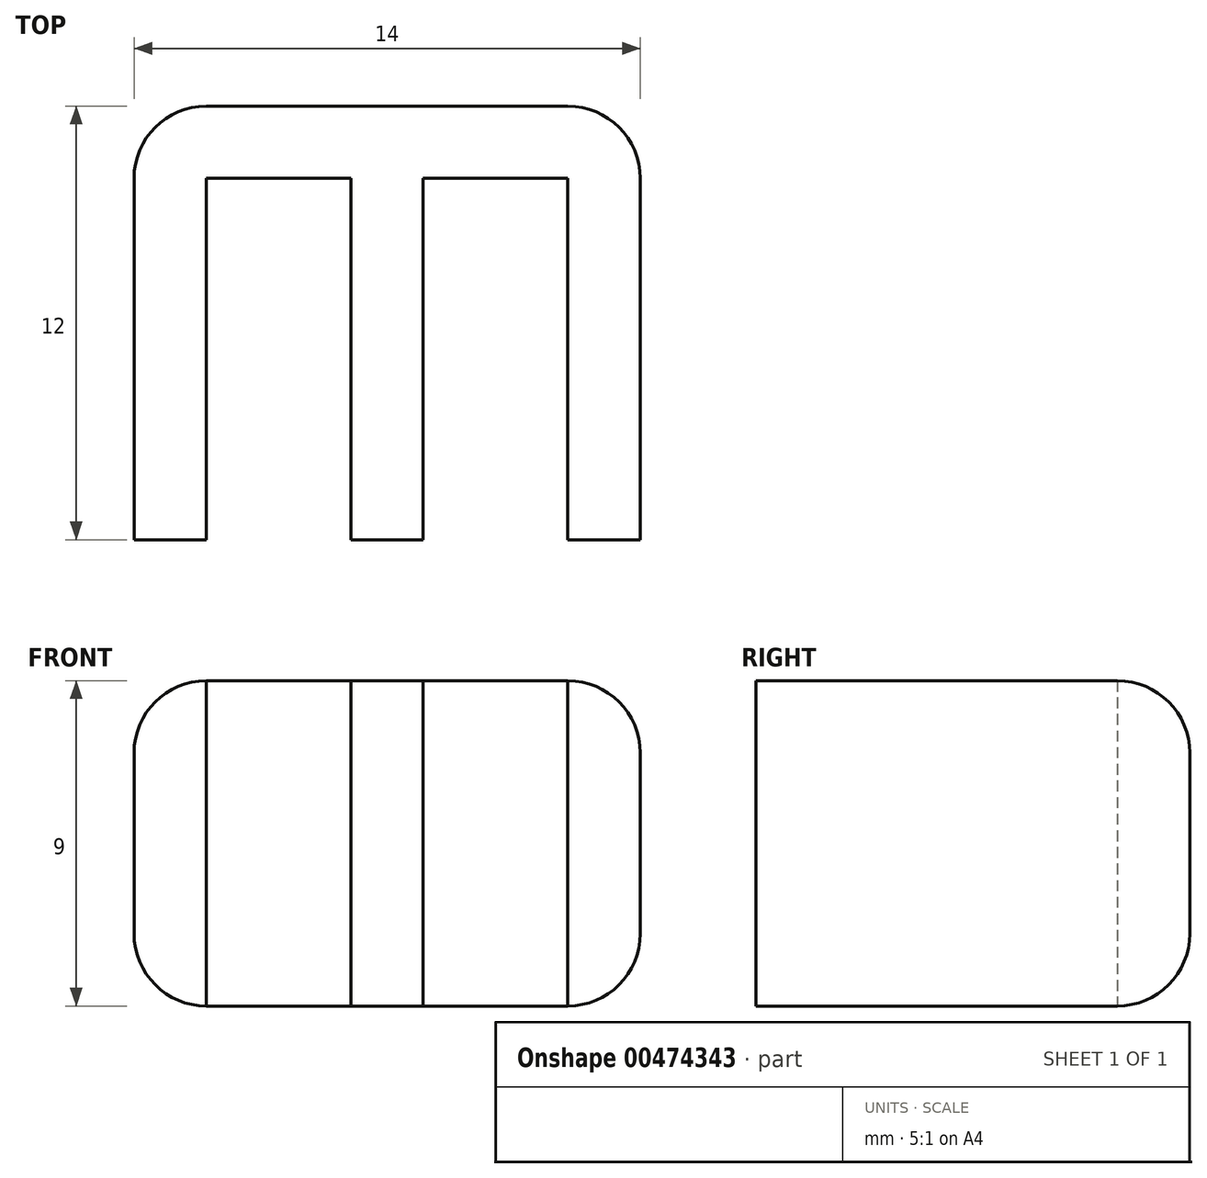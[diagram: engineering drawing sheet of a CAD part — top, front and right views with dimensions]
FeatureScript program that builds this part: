
annotation { "Feature Type Name" : "Feature", "Feature Type Description" : "" }
export const myFeature = defineFeature(function(context is Context, id is Id, definition is map)
    precondition{}
    {
        {
            var Q0;
            Q0=qCreatedBy(makeId("Top.planeOp"),FACE);
            var sketch = newSketch(context, id + "F0", { "sketchPlane" : qUnion([Q0])});
            skLineSegment(sketch, "E0.bottom", {"start": v(0, 0) * mm, "end": v(7, 0) * mm});
            skLineSegment(sketch, "E0.top", {"start": v(0, 12) * mm, "end": v(7, 12) * mm});
            skLineSegment(sketch, "E0.left", {"start": v(0, 0) * mm, "end": v(0, 12) * mm});
            skLineSegment(sketch, "E0.right", {"start": v(7, 0) * mm, "end": v(7, 12) * mm});
            skLineSegment(sketch, "E1.bottom", {"start": v(1, 0) * mm, "end": v(5, 0) * mm});
            skLineSegment(sketch, "E1.top", {"start": v(1, 10) * mm, "end": v(5, 10) * mm});
            skLineSegment(sketch, "E1.left", {"start": v(1, 0) * mm, "end": v(1, 10) * mm});
            skLineSegment(sketch, "E1.right", {"start": v(5, 0) * mm, "end": v(5, 10) * mm});
            skSolve(sketch);
        }
        {
            var Q0;
            Q0=makeQuery(id+"F0.imprint","IMPRINT",FACE,{"disambiguationData":[TD([[makeQuery(id+"F0.imprint","IMPRINT",EDGE,{"derivedFrom":sQuery(id+"F0.wireOp",EDGE,"E0.top")}),-1.0]])]});
            extrude(context, id + "F1", {"entities" : qUnion([Q0]), "depth" : 2.5 * mm, "offsetDistance" : 25 * mm});
        }
        {
            var Q0;
            Q0=makeQuery(id+"F0.imprint","IMPRINT",FACE,{"disambiguationData":[TD([[makeQuery(id+"F0.imprint","IMPRINT",EDGE,{"derivedFrom":sQuery(id+"F0.wireOp",EDGE,"E1.bottom")}),1.0]])]});
            var Q1;
            Q1=makeQuery(id+"F0.imprint","IMPRINT",FACE,{"disambiguationData":[TD([[makeQuery(id+"F0.imprint","IMPRINT",EDGE,{"derivedFrom":sQuery(id+"F0.wireOp",EDGE,"E0.top")}),-1.0]])]});
            extrude(context, id + "F2", {"entities" : qUnion([Q0, Q1]), "operationType" : NewBodyOperationType.ADD, "oppositeDirection" : true, "depth" : 2 * mm, "offsetDistance" : 25 * mm});
        }
        {
            var Q0;
            Q0=makeQuery(id+"F1.opExtrude","SWEPT_BODY",BODY,{"disambiguationData":[OSD([sQuery(id+"F0.wireOp",EDGE,"E0.bottom"),sQuery(id+"F0.wireOp",EDGE,"E0.top"),sQuery(id+"F0.wireOp",EDGE,"E0.left"),sQuery(id+"F0.wireOp",EDGE,"E0.right"),sQuery(id+"F0.wireOp",EDGE,"E1.top"),sQuery(id+"F0.wireOp",EDGE,"E1.left"),sQuery(id+"F0.wireOp",EDGE,"E1.right")])]});
            var Q1;
            {var subQ0=sQuery(id+"F0.wireOp",EDGE,"E0.left");Q1=makeQuery(id+"F2.boolean.opBoolean","MERGE",FACE,{"derivedFrom":[makeQuery(id+"F1.opExtrude","SWEPT_FACE",FACE,{"disambiguationData":[OSD([subQ0])]}),makeQuery(id+"F2.opExtrude","SWEPT_FACE",FACE,{"disambiguationData":[OSD([subQ0])]})]});}
            var Q2;
            {var subQ0=sQuery(id+"F0.wireOp",EDGE,"E0.left");Q2=makeQuery(id+"F2.boolean.opBoolean","MERGE",FACE,{"derivedFrom":[makeQuery(id+"F1.opExtrude","SWEPT_FACE",FACE,{"disambiguationData":[OSD([subQ0])]}),makeQuery(id+"F2.opExtrude","SWEPT_FACE",FACE,{"disambiguationData":[OSD([subQ0])]})]});}
            mirror(context, id + "F3", {"operationType" : NewBodyOperationType.ADD, "entities" : qUnion([Q0]), "mirrorPlane" : qUnion([Q1, Q2])});
        }
        {
            var Q0;
            Q0=makeQuery(id+"F1.opExtrude","SWEPT_BODY",BODY,{"disambiguationData":[OSD([sQuery(id+"F0.wireOp",EDGE,"E0.bottom"),sQuery(id+"F0.wireOp",EDGE,"E0.top"),sQuery(id+"F0.wireOp",EDGE,"E0.left"),sQuery(id+"F0.wireOp",EDGE,"E0.right"),sQuery(id+"F0.wireOp",EDGE,"E1.top"),sQuery(id+"F0.wireOp",EDGE,"E1.left"),sQuery(id+"F0.wireOp",EDGE,"E1.right")])]});
            var Q1;
            {var subQ0=makeQuery(id+"F1.opExtrude","CAP_FACE",FACE,{"disambiguationData":[OSD([sQuery(id+"F0.wireOp",EDGE,"E0.bottom"),sQuery(id+"F0.wireOp",EDGE,"E0.top"),sQuery(id+"F0.wireOp",EDGE,"E0.left"),sQuery(id+"F0.wireOp",EDGE,"E0.right"),sQuery(id+"F0.wireOp",EDGE,"E1.top"),sQuery(id+"F0.wireOp",EDGE,"E1.left"),sQuery(id+"F0.wireOp",EDGE,"E1.right")])],"isStart":false});Q1=makeQuery(id+"F3.boolean.opBoolean","MERGE",FACE,{"derivedFrom":[subQ0,makeQuery(id+"F3.opPattern","COPY",FACE,{"derivedFrom":subQ0,"instanceName":"1"})]});}
            mirror(context, id + "F4", {"operationType" : NewBodyOperationType.ADD, "entities" : qUnion([Q0]), "mirrorPlane" : qUnion([Q1])});
        }
        {
            var Q0;
            {var subQ0=makeQuery(id+"F2.opExtrude","CAP_EDGE",EDGE,{"disambiguationData":[OSD([sQuery(id+"F0.wireOp",EDGE,"E0.top")])],"isStart":false});Q0=makeQuery(id+"F4.opPattern","COPY",EDGE,{"derivedFrom":makeQuery(id+"F3.boolean.opBoolean","MERGE",EDGE,{"derivedFrom":[subQ0,makeQuery(id+"F3.opPattern","COPY",EDGE,{"derivedFrom":subQ0,"instanceName":"1"})]}),"instanceName":"1"});}
            var Q1;
            {var subQ0=sQuery(id+"F0.wireOp",EDGE,"E0.right");var subQ1=sQuery(id+"F0.wireOp",EDGE,"E0.top");var subQ2=makeQuery(id+"F2.boolean.opBoolean","MERGE",EDGE,{"derivedFrom":[makeQuery(id+"F1.opExtrude","SWEPT_EDGE",EDGE,{"disambiguationData":[OSD([subQ1,subQ0])]}),makeQuery(id+"F2.opExtrude","SWEPT_EDGE",EDGE,{"disambiguationData":[OSD([subQ1,subQ0])]})]});Q1=makeQuery(id+"F4.boolean.opBoolean","MERGE",EDGE,{"derivedFrom":[subQ2,makeQuery(id+"F4.opPattern","COPY",EDGE,{"derivedFrom":subQ2,"instanceName":"1"})]});}
            var Q2;
            {var subQ0=makeQuery(id+"F2.opExtrude","CAP_EDGE",EDGE,{"disambiguationData":[OSD([sQuery(id+"F0.wireOp",EDGE,"E0.top")])],"isStart":false});Q2=makeQuery(id+"F3.boolean.opBoolean","MERGE",EDGE,{"derivedFrom":[subQ0,makeQuery(id+"F3.opPattern","COPY",EDGE,{"derivedFrom":subQ0,"instanceName":"1"})]});}
            var Q3;
            {var subQ0=sQuery(id+"F0.wireOp",EDGE,"E0.right");var subQ1=sQuery(id+"F0.wireOp",EDGE,"E0.top");var subQ2=makeQuery(id+"F3.opPattern","COPY",EDGE,{"derivedFrom":makeQuery(id+"F2.boolean.opBoolean","MERGE",EDGE,{"derivedFrom":[makeQuery(id+"F1.opExtrude","SWEPT_EDGE",EDGE,{"disambiguationData":[OSD([subQ1,subQ0])]}),makeQuery(id+"F2.opExtrude","SWEPT_EDGE",EDGE,{"disambiguationData":[OSD([subQ1,subQ0])]})]}),"instanceName":"1"});Q3=makeQuery(id+"F4.boolean.opBoolean","MERGE",EDGE,{"derivedFrom":[subQ2,makeQuery(id+"F4.opPattern","COPY",EDGE,{"derivedFrom":subQ2,"instanceName":"1"})]});}
            var Q4;
            Q4=makeQuery(id+"F4.opPattern","COPY",EDGE,{"derivedFrom":makeQuery(id+"F2.opExtrude","CAP_EDGE",EDGE,{"disambiguationData":[OSD([sQuery(id+"F0.wireOp",EDGE,"E0.right")])],"isStart":false}),"instanceName":"1"});
            var Q5;
            Q5=makeQuery(id+"F4.opPattern","COPY",EDGE,{"derivedFrom":makeQuery(id+"F3.opPattern","COPY",EDGE,{"derivedFrom":makeQuery(id+"F2.opExtrude","CAP_EDGE",EDGE,{"disambiguationData":[OSD([sQuery(id+"F0.wireOp",EDGE,"E0.right")])],"isStart":false}),"instanceName":"1"}),"instanceName":"1"});
            var Q6;
            Q6=makeQuery(id+"F2.opExtrude","CAP_EDGE",EDGE,{"disambiguationData":[OSD([sQuery(id+"F0.wireOp",EDGE,"E0.right")])],"isStart":false});
            var Q7;
            Q7=makeQuery(id+"F3.opPattern","COPY",EDGE,{"derivedFrom":makeQuery(id+"F2.opExtrude","CAP_EDGE",EDGE,{"disambiguationData":[OSD([sQuery(id+"F0.wireOp",EDGE,"E0.right")])],"isStart":false}),"instanceName":"1"});
            fillet(context, id + "F5", {"entities" : qUnion([Q0, Q1, Q2, Q3, Q4, Q5, Q6, Q7]), "radius" : 2 * mm, "tangentPropagation" : true, "allowEdgeOverflow" : false});
        }
    });
